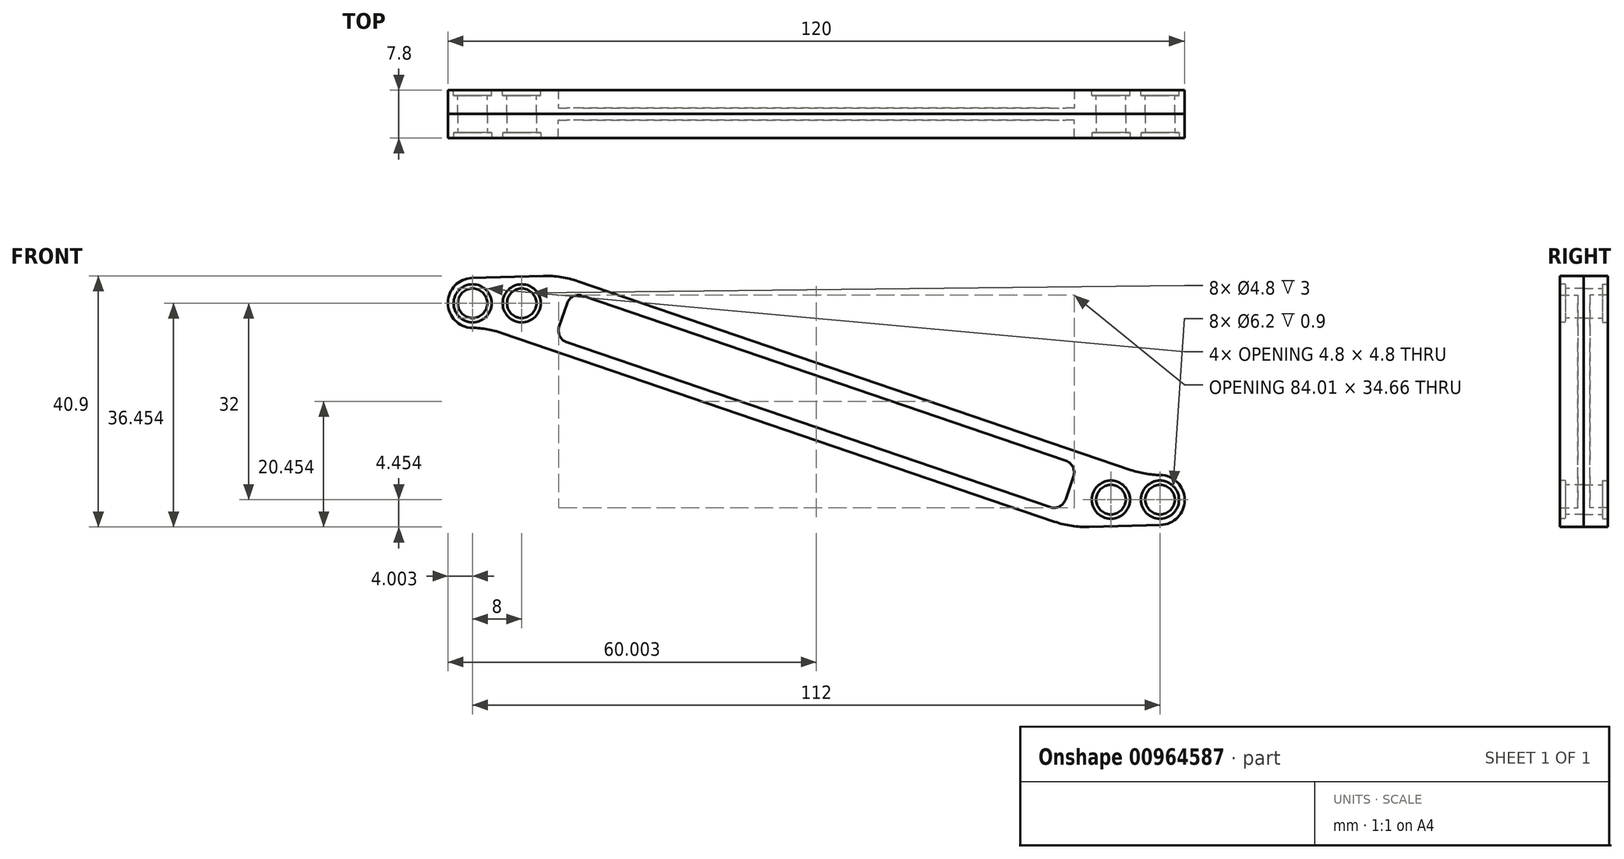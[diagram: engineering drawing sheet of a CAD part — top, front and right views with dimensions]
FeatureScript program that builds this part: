
annotation { "Feature Type Name" : "Feature", "Feature Type Description" : "" }
export const myFeature = defineFeature(function(context is Context, id is Id, definition is map)
    precondition{}
    {
        {
            var Q0;
            Q0=qCreatedBy(makeId("Front.planeOp"),FACE);
            var sketch = newSketch(context, id + "F0", { "sketchPlane" : qUnion([Q0])});
            skLineSegment(sketch, "E0.bottom", {"start": v(9.52, 5.67) * mm, "end": v(29.52, 5.67) * mm});
            skLineSegment(sketch, "E0.top", {"start": v(9.52, -2.33) * mm, "end": v(29.52, -2.33) * mm});
            skLineSegment(sketch, "E0.left", {"start": v(9.52, 5.67) * mm, "end": v(9.52, -2.33) * mm});
            skLineSegment(sketch, "E0.right", {"start": v(29.52, 5.67) * mm, "end": v(29.52, -2.33) * mm});
            skLineSegment(sketch, "E1.bottom", {"start": v(109.52, -26.33) * mm, "end": v(129.52, -26.33) * mm});
            skLineSegment(sketch, "E1.top", {"start": v(109.52, -34.33) * mm, "end": v(129.52, -34.33) * mm});
            skLineSegment(sketch, "E1.left", {"start": v(109.52, -26.33) * mm, "end": v(109.52, -34.33) * mm});
            skLineSegment(sketch, "E1.right", {"start": v(129.52, -26.33) * mm, "end": v(129.52, -34.33) * mm});
            skLineSegment(sketch, "E2", {"start": v(2.63, 1.67) * mm, "end": v(40.42, 1.67) * mm, "construction": true});
            skLineSegment(sketch, "E3", {"start": v(38.6, -30.33) * mm, "end": v(72.07, -30.33) * mm, "construction": true});
            skPoint(sketch, "E4", {"position": v(13.52, 1.67) * mm});
            skPoint(sketch, "E5", {"position": v(21.52, 1.67) * mm});
            skPoint(sketch, "E6", {"position": v(117.52, -30.33) * mm});
            skPoint(sketch, "E7", {"position": v(125.52, -30.33) * mm});
            skLineSegment(sketch, "E8", {"start": v(27.98, 6.2) * mm, "end": v(123.23, -26.33) * mm});
            skLineSegment(sketch, "E9", {"start": v(111.07, -34.85) * mm, "end": v(15.82, -2.33) * mm});
            skLineSegment(sketch, "E10", {"start": v(29.56, 3.55) * mm, "end": v(112.07, -24.63) * mm});
            skLineSegment(sketch, "E11", {"start": v(112.07, -24.63) * mm, "end": v(109.49, -32.2) * mm});
            skLineSegment(sketch, "E12", {"start": v(109.49, -32.2) * mm, "end": v(26.97, -4.02) * mm});
            skLineSegment(sketch, "E13", {"start": v(26.97, -4.02) * mm, "end": v(29.56, 3.55) * mm});
            skCircle(sketch, "E14", {"center": v(21.52, 1.67) * mm, "radius": 7 * mm, "construction": true});
            skCircle(sketch, "E15", {"center": v(117.52, -30.33) * mm, "radius": 7 * mm, "construction": true});
            skLineSegment(sketch, "E16", {"start": v(21.52, 1.67) * mm, "end": v(21.52, 15.58) * mm, "construction": true});
            skLineSegment(sketch, "E17", {"start": v(27.98, 6.2) * mm, "end": v(9.52, 5.67) * mm});
            skLineSegment(sketch, "E18", {"start": v(15.82, -2.33) * mm, "end": v(27.98, 6.2) * mm, "construction": true});
            skLineSegment(sketch, "E19", {"start": v(123.23, -26.33) * mm, "end": v(104.25, -39.63) * mm, "construction": true});
            skLineSegment(sketch, "E20", {"start": v(129.52, -34.33) * mm, "end": v(111.07, -34.85) * mm});
            skSolve(sketch);
        }
        {
            var Q0;
            {var subQ7=sQuery(id+"F0.wireOp",EDGE,"E0.bottom");Q0=makeQuery(id+"F0.imprint","IMPRINT",FACE,{"disambiguationData":[TD([[makeQuery(id+"F0.imprint","IMPRINT",EDGE,{"derivedFrom":subQ7}),-1.0]])]});}
            var Q1;
            {var subQ5=sQuery(id+"F0.wireOp",EDGE,"E8");Q1=makeQuery(id+"F0.imprint","IMPRINT",FACE,{"disambiguationData":[TD([[makeQuery(id+"F0.imprint","IMPRINT",EDGE,{"derivedFrom":subQ5}),-1.0]])]});}
            var Q2;
            {var subQ5=sQuery(id+"F0.wireOp",EDGE,"E9");Q2=makeQuery(id+"F0.imprint","IMPRINT",FACE,{"disambiguationData":[TD([[makeQuery(id+"F0.imprint","IMPRINT",EDGE,{"derivedFrom":subQ5}),-1.0]])]});}
            var Q3;
            {var subQ11=sQuery(id+"F0.wireOp",EDGE,"E0.top");var subQ13=sQuery(id+"F0.wireOp",EDGE,"E0.right");var subQ14=makeQuery(id+"F0.imprint","INTERSECT",VERTEX,{"derivedFrom":[subQ11,subQ13]});Q3=makeQuery(id+"F0.imprint","IMPRINT",FACE,{"disambiguationData":[TD([[makeQuery(id+"F0.imprint","IMPRINT",EDGE,{"disambiguationData":[TD([[subQ14,1.0]])],"derivedFrom":subQ11}),-1.0]])]});}
            var Q4;
            {var subQ0=sQuery(id+"F0.wireOp",EDGE,"E1.left");var subQ1=sQuery(id+"F0.wireOp",EDGE,"E1.bottom");var subQ2=makeQuery(id+"F0.imprint","INTERSECT",VERTEX,{"derivedFrom":[subQ1,subQ0]});Q4=makeQuery(id+"F0.imprint","IMPRINT",FACE,{"disambiguationData":[TD([[makeQuery(id+"F0.imprint","IMPRINT",EDGE,{"disambiguationData":[TD([[subQ2,-1.0]])],"derivedFrom":subQ1}),-1.0]])]});}
            var Q5;
            {var subQ1=sQuery(id+"F0.wireOp",EDGE,"E1.top");Q5=makeQuery(id+"F0.imprint","IMPRINT",FACE,{"disambiguationData":[TD([[makeQuery(id+"F0.imprint","IMPRINT",EDGE,{"derivedFrom":subQ1}),1.0]])]});}
            var Q6;
            {var subQ0=sQuery(id+"F0.wireOp",EDGE,"E0.right");var subQ1=sQuery(id+"F0.wireOp",EDGE,"E0.top");var subQ2=makeQuery(id+"F0.imprint","INTERSECT",VERTEX,{"derivedFrom":[subQ1,subQ0]});Q6=makeQuery(id+"F0.imprint","IMPRINT",FACE,{"disambiguationData":[TD([[makeQuery(id+"F0.imprint","IMPRINT",EDGE,{"disambiguationData":[TD([[subQ2,1.0]])],"derivedFrom":subQ1}),1.0]])]});}
            var Q7;
            {var subQ5=sQuery(id+"F0.wireOp",EDGE,"E8");var subQ6=sQuery(id+"F0.wireOp",EDGE,"E1.bottom");var subQ7=makeQuery(id+"F0.imprint","INTERSECT",VERTEX,{"derivedFrom":[subQ6,subQ5]});Q7=makeQuery(id+"F0.imprint","IMPRINT",FACE,{"disambiguationData":[TD([[makeQuery(id+"F0.imprint","IMPRINT",EDGE,{"disambiguationData":[TD([[subQ7,1.0]])],"derivedFrom":subQ6}),1.0]])]});}
            var Q8;
            {var subQ5=sQuery(id+"F0.wireOp",EDGE,"E9");var subQ7=sQuery(id+"F0.wireOp",EDGE,"E0.top");var subQ8=makeQuery(id+"F0.imprint","INTERSECT",VERTEX,{"derivedFrom":[subQ7,subQ5]});Q8=makeQuery(id+"F0.imprint","IMPRINT",FACE,{"disambiguationData":[TD([[makeQuery(id+"F0.imprint","IMPRINT",EDGE,{"disambiguationData":[TD([[subQ8,-1.0]])],"derivedFrom":subQ7}),-1.0]])]});}
            extrude(context, id + "F1", {"entities" : qUnion([Q0, Q1, Q2, Q3, Q4, Q5, Q6, Q7, Q8]), "depth" : 3.9 * mm, "offsetDistance" : 25 * mm});
        }
        {
            var Q0;
            {var subQ11=sQuery(id+"F0.wireOp",EDGE,"E0.top");var subQ13=sQuery(id+"F0.wireOp",EDGE,"E0.right");var subQ14=makeQuery(id+"F0.imprint","INTERSECT",VERTEX,{"derivedFrom":[subQ11,subQ13]});Q0=makeQuery(id+"F0.imprint","IMPRINT",FACE,{"disambiguationData":[TD([[makeQuery(id+"F0.imprint","IMPRINT",EDGE,{"disambiguationData":[TD([[subQ14,1.0]])],"derivedFrom":subQ11}),-1.0]])]});}
            var Q1;
            {var subQ0=sQuery(id+"F0.wireOp",EDGE,"E1.left");var subQ1=sQuery(id+"F0.wireOp",EDGE,"E1.bottom");var subQ2=makeQuery(id+"F0.imprint","INTERSECT",VERTEX,{"derivedFrom":[subQ1,subQ0]});Q1=makeQuery(id+"F0.imprint","IMPRINT",FACE,{"disambiguationData":[TD([[makeQuery(id+"F0.imprint","IMPRINT",EDGE,{"disambiguationData":[TD([[subQ2,-1.0]])],"derivedFrom":subQ1}),-1.0]])]});}
            var Q2;
            {var subQ0=sQuery(id+"F0.wireOp",EDGE,"E0.right");var subQ1=sQuery(id+"F0.wireOp",EDGE,"E0.top");var subQ2=makeQuery(id+"F0.imprint","INTERSECT",VERTEX,{"derivedFrom":[subQ1,subQ0]});Q2=makeQuery(id+"F0.imprint","IMPRINT",FACE,{"disambiguationData":[TD([[makeQuery(id+"F0.imprint","IMPRINT",EDGE,{"disambiguationData":[TD([[subQ2,1.0]])],"derivedFrom":subQ1}),1.0]])]});}
            extrude(context, id + "F2", {"entities" : qUnion([Q0, Q1, Q2]), "operationType" : NewBodyOperationType.REMOVE, "depth" : (3.9 - 1) * mm, "offsetDistance" : 25 * mm});
        }
        {
            var Q0;
            Q0=sQuery(id+"F0.wireOp",VERTEX,"E7");
            var Q1;
            Q1=sQuery(id+"F0.wireOp",VERTEX,"E6");
            var Q2;
            Q2=sQuery(id+"F0.wireOp",VERTEX,"E4");
            var Q3;
            Q3=sQuery(id+"F0.wireOp",VERTEX,"E5");
            var Q4;
            Q4=makeQuery(id+"F1.opExtrude","SWEPT_BODY",BODY,{"disambiguationData":[OSD([sQuery(id+"F0.wireOp",EDGE,"E0.bottom"),sQuery(id+"F0.wireOp",EDGE,"E0.top"),sQuery(id+"F0.wireOp",EDGE,"E0.left"),sQuery(id+"F0.wireOp",EDGE,"E1.bottom"),sQuery(id+"F0.wireOp",EDGE,"E1.top"),sQuery(id+"F0.wireOp",EDGE,"E1.right"),sQuery(id+"F0.wireOp",EDGE,"E8"),sQuery(id+"F0.wireOp",EDGE,"E9")])]});
            hole(context, id + "F3", {"style" : HoleStyle.C_BORE, "endStyle" : HoleEndStyle.THROUGH, "oppositeDirection" : true, "holeDiameter" : 4.8 * mm, "cBoreDiameter" : 6.2 * mm, "cBoreDepth" : 0.9 * mm, "majorDiameter" : 5 * mm, "isTappedThrough" : true, "tappedDepth" : 12 * mm, "tapClearance" : 3, "locations" : qUnion([Q0, Q1, Q2, Q3]), "scope" : qUnion([Q4])});
        }
        {
            var Q0;
            Q0=makeQuery(id+"F1.opExtrude","SWEPT_EDGE",EDGE,{"disambiguationData":[OSD([sQuery(id+"F0.wireOp",EDGE,"E0.top"),sQuery(id+"F0.wireOp",EDGE,"E9")])]});
            var Q1;
            Q1=makeQuery(id+"F1.opExtrude","SWEPT_EDGE",EDGE,{"disambiguationData":[OSD([sQuery(id+"F0.wireOp",EDGE,"E0.bottom"),sQuery(id+"F0.wireOp",EDGE,"E0.right"),sQuery(id+"F0.wireOp",EDGE,"E8")])]});
            var Q2;
            Q2=makeQuery(id+"F1.opExtrude","SWEPT_EDGE",EDGE,{"disambiguationData":[OSD([sQuery(id+"F0.wireOp",EDGE,"E1.bottom"),sQuery(id+"F0.wireOp",EDGE,"E8")])]});
            var Q3;
            Q3=makeQuery(id+"F1.opExtrude","SWEPT_EDGE",EDGE,{"disambiguationData":[OSD([sQuery(id+"F0.wireOp",EDGE,"E1.top"),sQuery(id+"F0.wireOp",EDGE,"E1.left"),sQuery(id+"F0.wireOp",EDGE,"E9")])]});
            var Q4;
            Q4=makeQuery(id+"F1.opExtrude","SWEPT_EDGE",EDGE,{"disambiguationData":[OSD([sQuery(id+"F0.wireOp",EDGE,"E17"),sQuery(id+"F0.wireOp",EDGE,"K8q94cl6-8PaB-G3ml-sR8P-GxQxIrCVvqRL")])]});
            fillet(context, id + "F4", {"entities" : qUnion([Q0, Q1, Q2, Q3, Q4]), "radius" : 16 * mm, "tangentPropagation" : true, "allowEdgeOverflow" : false});
        }
        {
            var Q0;
            Q0=makeQuery(id+"F1.opExtrude","SWEPT_EDGE",EDGE,{"disambiguationData":[OSD([sQuery(id+"F0.wireOp",EDGE,"E0.top"),sQuery(id+"F0.wireOp",EDGE,"E0.left")])]});
            var Q1;
            Q1=makeQuery(id+"F1.opExtrude","SWEPT_EDGE",EDGE,{"disambiguationData":[OSD([sQuery(id+"F0.wireOp",EDGE,"E0.bottom"),sQuery(id+"F0.wireOp",EDGE,"E0.left")])]});
            var Q2;
            Q2=makeQuery(id+"F1.opExtrude","SWEPT_EDGE",EDGE,{"disambiguationData":[OSD([sQuery(id+"F0.wireOp",EDGE,"E1.top"),sQuery(id+"F0.wireOp",EDGE,"E1.right")])]});
            var Q3;
            Q3=makeQuery(id+"F1.opExtrude","SWEPT_EDGE",EDGE,{"disambiguationData":[OSD([sQuery(id+"F0.wireOp",EDGE,"E1.bottom"),sQuery(id+"F0.wireOp",EDGE,"E1.right")])]});
            fillet(context, id + "F5", {"entities" : qUnion([Q0, Q1, Q2, Q3]), "radius" : 4 * mm, "tangentPropagation" : true, "allowEdgeOverflow" : false});
        }
        {
            var Q0;
            Q0=makeQuery(id+"F2.boolean.opBoolean","COPY",EDGE,{"derivedFrom":makeQuery(id+"F2.opExtrude","SWEPT_EDGE",EDGE,{"disambiguationData":[OSD([sQuery(id+"F0.wireOp",EDGE,"E10"),sQuery(id+"F0.wireOp",EDGE,"E13")])]})});
            var Q1;
            Q1=makeQuery(id+"F2.boolean.opBoolean","COPY",EDGE,{"derivedFrom":makeQuery(id+"F2.opExtrude","SWEPT_EDGE",EDGE,{"disambiguationData":[OSD([sQuery(id+"F0.wireOp",EDGE,"E10"),sQuery(id+"F0.wireOp",EDGE,"E11")])]})});
            var Q2;
            Q2=makeQuery(id+"F2.boolean.opBoolean","COPY",EDGE,{"derivedFrom":makeQuery(id+"F2.opExtrude","SWEPT_EDGE",EDGE,{"disambiguationData":[OSD([sQuery(id+"F0.wireOp",EDGE,"E11"),sQuery(id+"F0.wireOp",EDGE,"E12")])]})});
            var Q3;
            Q3=makeQuery(id+"F2.boolean.opBoolean","COPY",EDGE,{"derivedFrom":makeQuery(id+"F2.opExtrude","SWEPT_EDGE",EDGE,{"disambiguationData":[OSD([sQuery(id+"F0.wireOp",EDGE,"E12"),sQuery(id+"F0.wireOp",EDGE,"E13")])]})});
            fillet(context, id + "F6", {"entities" : qUnion([Q0, Q1, Q2, Q3]), "radius" : 2 * mm, "tangentPropagation" : true, "allowEdgeOverflow" : false});
        }
        {
            var Q0;
            Q0=makeQuery(id+"F1.opExtrude","SWEPT_BODY",BODY,{"disambiguationData":[OSD([sQuery(id+"F0.wireOp",EDGE,"E0.bottom"),sQuery(id+"F0.wireOp",EDGE,"E0.top"),sQuery(id+"F0.wireOp",EDGE,"E0.left"),sQuery(id+"F0.wireOp",EDGE,"E1.bottom"),sQuery(id+"F0.wireOp",EDGE,"E1.top"),sQuery(id+"F0.wireOp",EDGE,"E1.right"),sQuery(id+"F0.wireOp",EDGE,"E8"),sQuery(id+"F0.wireOp",EDGE,"E9")])]});
            var Q1;
            Q1=makeQuery(id+"F1.opExtrude","CAP_FACE",FACE,{"disambiguationData":[OSD([sQuery(id+"F0.wireOp",EDGE,"E0.bottom"),sQuery(id+"F0.wireOp",EDGE,"E0.top"),sQuery(id+"F0.wireOp",EDGE,"E0.left"),sQuery(id+"F0.wireOp",EDGE,"E1.bottom"),sQuery(id+"F0.wireOp",EDGE,"E1.top"),sQuery(id+"F0.wireOp",EDGE,"E1.right"),sQuery(id+"F0.wireOp",EDGE,"E8"),sQuery(id+"F0.wireOp",EDGE,"E9")])],"isStart":false});
            mirror(context, id + "F7", {"entities" : qUnion([Q0]), "mirrorPlane" : qUnion([Q1])});
        }
    });
